# Revit family: IS_Joy_A7387_BIM_GB
name_source: partatom
category: Plumbing Fixtures
revit_build: Autodesk Revit 2017 (Build: 20160225_1515(x64)
units: mm (PartAtom-declared; Revit-internal decimal feet)

## family parameters
Always vertical = No
Cut with Voids When Loaded = No
OmniClass Number = 23.45.55.00
OmniClass Title = Sanitary Faucets, Wastes
Part Type = Normal
Room Calculation Point = No
Round Connector Dimension = Use Diameter
Shared = No
Work Plane-Based = No

## types (4) — shared parameters
Accessories = https://www.idealstandard.co.uk
AssetType = Fixed
BIMObjectName = ISI_IdealStandard_Bath manual water supply sets_Joy_A7387
BarCode = 4015413346610
Brand = Ideal Standard
CurrencyUnit = £
Description = JOY freestanding bath spout with rigid pipe outlet with aerator. 780-790 mm Height. Available in four different finishes, Chrome (AA), Silver storm (GN) 386, Brushed gold (A2) and Magnetic grey (A5)
DistributedBy = Ideal Standard
DurationUnit = Years
ExpectedLife = 30
FaucetFunction = MIXED
FaucetOperation = OTHER
FaucetType = OTHER
Features = freestanding bath spout with rigid pipe outlet with aerator. 780-790 mm Height. Available in four different finishes, Chrome (AA), Silver storm (GN) 386, Brushed gold (A2) and Magnetic grey (A5)
Help = https://www.idealstandard.co.uk
IfcExportAs = IfcValveType
IfcExportType = FAUCET
Installation instructions = https://www.idealspec.co.uk
InstallationInstructions = https://www.idealstandard.co.uk
IsBuiltIn = No
MaintenanceInformation = https://www.idealstandard.co.uk
Manufacturer = Ideal Standard
ManufacturerURL = https://www.idealstandard.co.uk
Material = Brass
ModelNumber = A7387
NBS Reference Code = 45-35-70/315
NBS Reference Description = Water supply fittings for baths
Name = Bath manual water supply sets_Joy_A7387_IdealStandard
NettWeight = 0
Product certification = https://www.idealstandard.co.uk
Product group = SPOUT
ProductInformation = https://www.idealspec.co.uk
Shape = Sculptured
Size = 130 x 339 x 959 mm
Space = Internal
SpareParts = https://www.idealspec.co.uk
SustainabilityPerformance = https://www.idealspec.co.uk
TestPressure = 10 Bar
URL = https://www.idealstandard.co.uk
Uniclass 2015 Code = Pr_40_20_87_07
Uniclass 2015 Name = Bath manual water supply sets
Uniclass2015Code = Pr_40_20_87_07
Uniclass2015Title = Bath manual water supply sets
Uniclass2015Version = v1.1
Version = 1
VolumeUnits = Litres
WRASURL = https://www.wras.co.uk
WarrantyDescription = Manufacturers Warranty
WarrantyDurationParts = 5
WarrantyDurationUnit = year
WarrantyGuarantorParts = https://www.idealspec.co.uk
WorkingPressure = 3bar
zero-valued in all types: InletConnectionSize, MaterialThickness, NominalDepth, NominalHeight, NominalLength, NominalWidth

## per-type parameters (varying)
| type | Color | Finish | MainColor | Model | ModelReference |
| A7387A2 - JOY BSH MXR FREESTANDING TUB SPT BR GOLD | Brushed Gold | Brushed Gold | Brushed Gold | A7387A2 | A7387A2 |
| A7387A5 - JOY BSH MXR FREESTANDNG TUB SPT MGN GREY | Magnetic grey | Magnetic grey | Magnetic grey | A7387A5 | A7387A5 |
| A7387AA - JOY BSH MXR FREESTANDING TUB SPT CHR | Chrome | Chrome | Chrome | A7387AA | A7387AA |
| A7387GN - JOY BSH MXR FREESTNDNG TUB SPT SILV STORM | Silver storm | Silver storm | Silver storm | A7387GN | A7387GN |

## geometry (parser evidence)
native form markers: Sweep x2
no freeform markers — native parametric forms only
